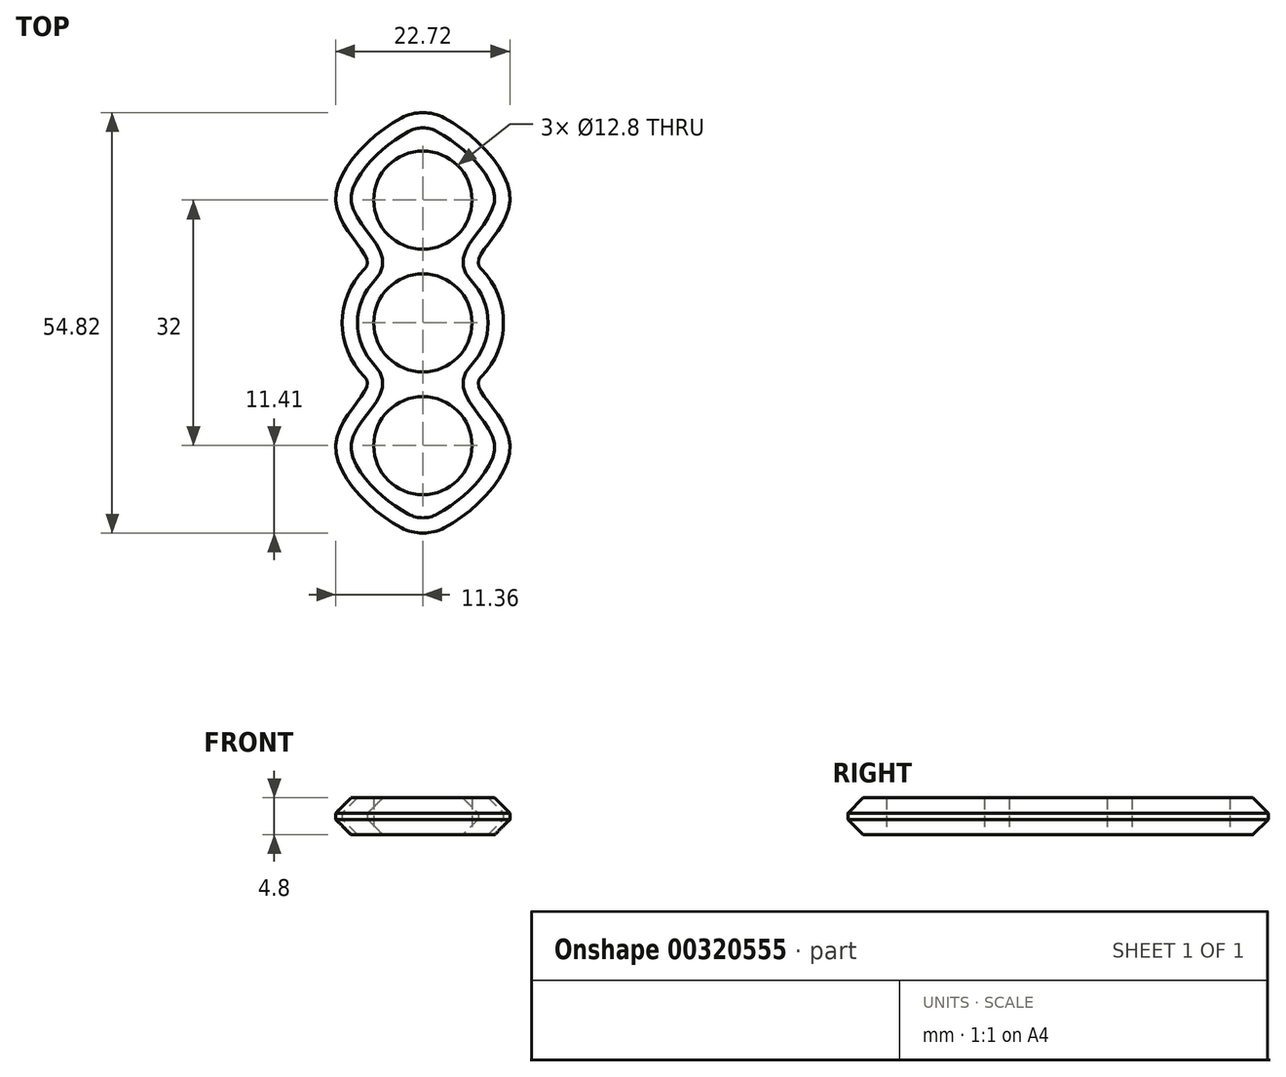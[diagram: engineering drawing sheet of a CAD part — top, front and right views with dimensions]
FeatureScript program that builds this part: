
annotation { "Feature Type Name" : "Feature", "Feature Type Description" : "" }
export const myFeature = defineFeature(function(context is Context, id is Id, definition is map)
    precondition{}
    {
        {
            var Q0;
            Q0=qCreatedBy(makeId("Top.planeOp"),FACE);
            var sketch = newSketch(context, id + "F0", { "sketchPlane" : qUnion([Q0])});
            skCircle(sketch, "E0", {"center": v(0, 0) * mm, "radius": 6.4 * mm});
            skCircle(sketch, "E1", {"center": v(0, 16) * mm, "radius": 6.4 * mm});
            skLineSegment(sketch, "E2", {"start": v(-23.82, 0) * mm, "end": v(26.02, 0) * mm, "construction": true});
            skLineSegment(sketch, "E3", {"start": v(0, 0) * mm, "end": v(0, 33.96) * mm, "construction": true});
            skFitSpline(sketch, "E4", {"points": [v(-12.4, 0) * mm, v(-7.2, 7.94) * mm, v(-11.36, 16.38) * mm, v(0, 27.74) * mm], "startDerivative": vector(12.33, 60.02) * mm, "endDerivative": vector(28.47, 4.14) * mm});
            skFitSpline(sketch, "E5.MirrorCS", {"points": [v(12.4, 0) * mm, v(7.2, 7.94) * mm, v(11.36, 16.38) * mm, v(0, 27.74) * mm], "startDerivative": vector(-12.33, 60.02) * mm, "endDerivative": vector(-28.47, 4.14) * mm});
            skFitSpline(sketch, "E6.MirrorCS", {"points": [v(-12.4, 0) * mm, v(-7.2, -7.94) * mm, v(-11.36, -16.38) * mm, v(0, -27.74) * mm], "startDerivative": vector(12.33, -60.02) * mm, "endDerivative": vector(28.47, -4.14) * mm});
            skFitSpline(sketch, "E7.MirrorCS", {"points": [v(12.4, 0) * mm, v(7.2, -7.94) * mm, v(11.36, -16.38) * mm, v(0, -27.74) * mm], "startDerivative": vector(-12.33, -60.02) * mm, "endDerivative": vector(-28.47, -4.14) * mm});
            skCircle(sketch, "E8.MirrorC", {"center": v(0, -16) * mm, "radius": 6.4 * mm});
            skSolve(sketch);
        }
        {
            var Q0;
            Q0=qSketchRegion(id+"F0",true);
            extrude(context, id + "F1", {"entities" : qUnion([Q0]), "depth" : 4.8 * mm});
        }
        {
            var Q0;
            Q0=makeQuery(id+"F1.opExtrude","SWEPT_EDGE",EDGE,{"disambiguationData":[OSD([sQuery(id+"F0.wireOp",EDGE,"E4"),sQuery(id+"F0.wireOp",EDGE,"E6.MirrorCS")])]});
            var Q1;
            Q1=makeQuery(id+"F1.opExtrude","SWEPT_EDGE",EDGE,{"disambiguationData":[OSD([sQuery(id+"F0.wireOp",EDGE,"E5.MirrorCS"),sQuery(id+"F0.wireOp",EDGE,"E7.MirrorCS")])]});
            fillet(context, id + "F2", {"entities" : qUnion([Q0, Q1]), "radius" : 10 * mm, "tangentPropagation" : true, "allowEdgeOverflow" : false});
        }
        {
            var Q0;
            Q0=makeQuery(id+"F1.opExtrude","SWEPT_EDGE",EDGE,{"disambiguationData":[OSD([sQuery(id+"F0.wireOp",EDGE,"E6.MirrorCS"),sQuery(id+"F0.wireOp",EDGE,"E7.MirrorCS")])]});
            var Q1;
            Q1=makeQuery(id+"F1.opExtrude","SWEPT_EDGE",EDGE,{"disambiguationData":[OSD([sQuery(id+"F0.wireOp",EDGE,"E4"),sQuery(id+"F0.wireOp",EDGE,"E5.MirrorCS")])]});
            fillet(context, id + "F3", {"entities" : qUnion([Q0, Q1]), "radius" : 6 * mm, "tangentPropagation" : true, "allowEdgeOverflow" : false});
        }
        {
            var Q0;
            Q0=makeQuery(id+"F1.opExtrude","CAP_EDGE",EDGE,{"disambiguationData":[OSD([sQuery(id+"F0.wireOp",EDGE,"E4")])],"isStart":false});
            var Q1;
            Q1=makeQuery(id+"F1.opExtrude","CAP_EDGE",EDGE,{"disambiguationData":[OSD([sQuery(id+"F0.wireOp",EDGE,"E4")])],"isStart":true});
            chamfer(context, id + "F4", {"entities" : qUnion([Q0, Q1]), "width" : 2 * mm, "tangentPropagation" : true});
        }
    });
